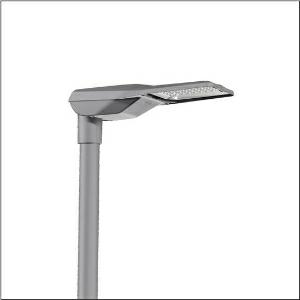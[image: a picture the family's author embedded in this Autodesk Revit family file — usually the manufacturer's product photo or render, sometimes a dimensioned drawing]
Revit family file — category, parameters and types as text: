
# Revit family: streetlight_sl_21_iq_mini___st0_5a_5xe2b31d08gb_9f53
name_source: partatom
category: Lighting Fixtures
units: mm (PartAtom-declared; Revit-internal decimal feet)

## family parameters
Cut with Voids When Loaded = No
Host = Face
Light Source = No
Part Type = Normal
Room Calculation Point = No
Round Connector Dimension = Use Diameter
Shared = No

## types (1)
- --- (1 x LED, 5680 lm, 37.1 W, 3000K)
    Apparent Load = 37 VA
    CIE Flux Codes = 41 75 97 100 100
    Color Rendering = 70
    Color Temperature = 3000K
    Default Elevation = 1800 mm
    Description = Streetlight SL 21 iQ mini, mast luminaire, primary light control with lens, of PMMA, primary optical cover: cover, of toughened safety glass, transparent, light distribution: ST0.5a, light emission: direct distribution, primary light characteristic: asymmetric, installation type: post-top, side-entry, LED, High Power LED, rated luminous flux: 5.680lm, luminous efficacy: 153lm/W, light colour: 730, colour temperature: 3000K, control gear: iQ-Comfort, control: Auto-Match, Temp-Guard, Lumen-Switch, Night-Set, Smart-Wire, Light-Fading, Desk-Remote (wireless, voltage-free reading and setting of iQ features in the workshop via application-optimized NFC function/RFID function), optimised constant luminous flux control (CLO 2.0), pre-setting: linear dimming characteristic, mains connection: 220..240V, AC, 50/60Hz, start of lifetime: 37W, end of service life: 39W, reduction: 18W, luminaire housing, of diecast aluminium, powder-coated, SITECO metallic grey (DB 702S), corrosivity category C5 high according to DIN EN ISO 12944, please order mast flange separately, inclination adjustable: 0°, 5°, 10°, 15°, sealing non-destructively replaceable, multi-level sealing system, length: 628mm, width: 235mm, height: 110mm, mast flange for spigot size: 42mm (side-entry): 5XC10008XM4, 60/48mm (side-entry/post-top): 5XC10108XM2, 76/60mm (side-entry/post-top): 5XC10108XM1, mounting height: 4..8m, protection rating (complete): IP66, insulation class (complete): insulation class II (safety insulation), certification: CE, ENEC, ENEC+, VDE, impact resistance: IK10, permissible operating ambient temperature for outdoor applications: -40..+50°C, standard-compliant lighting for roads and squares, packaging unit: 1 piece

Light Distribution: ST0.5a
    Height = 110 mm
    Lamp = 1 x LED
    Lamp Light Flux = 5680 lm
    Lamp Power = 37.1 W
    Lamp count = 1
    Length = 625 mm
    Luminous efficacy = 153 lm/W
    Manufacturer = Siteco
    ModVariant = No
    Model = 5XE2B31D08GB
    Number of Poles = 1
    OnlyDefault = Yes
    Power Factor = 1
    Product Name = Streetlight SL 21 iQ mini | ST0.5a
    Product group = mast luminaire | pylon top
    ProductGroupID = 6100
    Protection Class = Protection class II
    Protection Degree = IP 66
    RLX_Detail_Level = 1
    RLX_Emergency_Light_Flux = 0 lm
    RLX_Emergency_Type = 0
    RLX_Emergency_Type_DB = No
    RlxData = <blob elided: 37313 chars, md5=d602d302>
    Socket = socket
    Standby Power = 0 W
    System Light Flux = 5680 lm
    System Power = 37 W
    Type Comments = factory setting: luminous flux: 100 % | dim-lin: 254 | 385 mA
    Type Image = l_1003519.jpg
    URL = http://relux.com
    VarID = @adj_188877
    Voltage = 0 V
    Weight = 0.00 kg
    Width = 234 mm

## geometry (parser evidence)
native form markers: Blend x4, Sweep x10
no freeform markers — native parametric forms only
